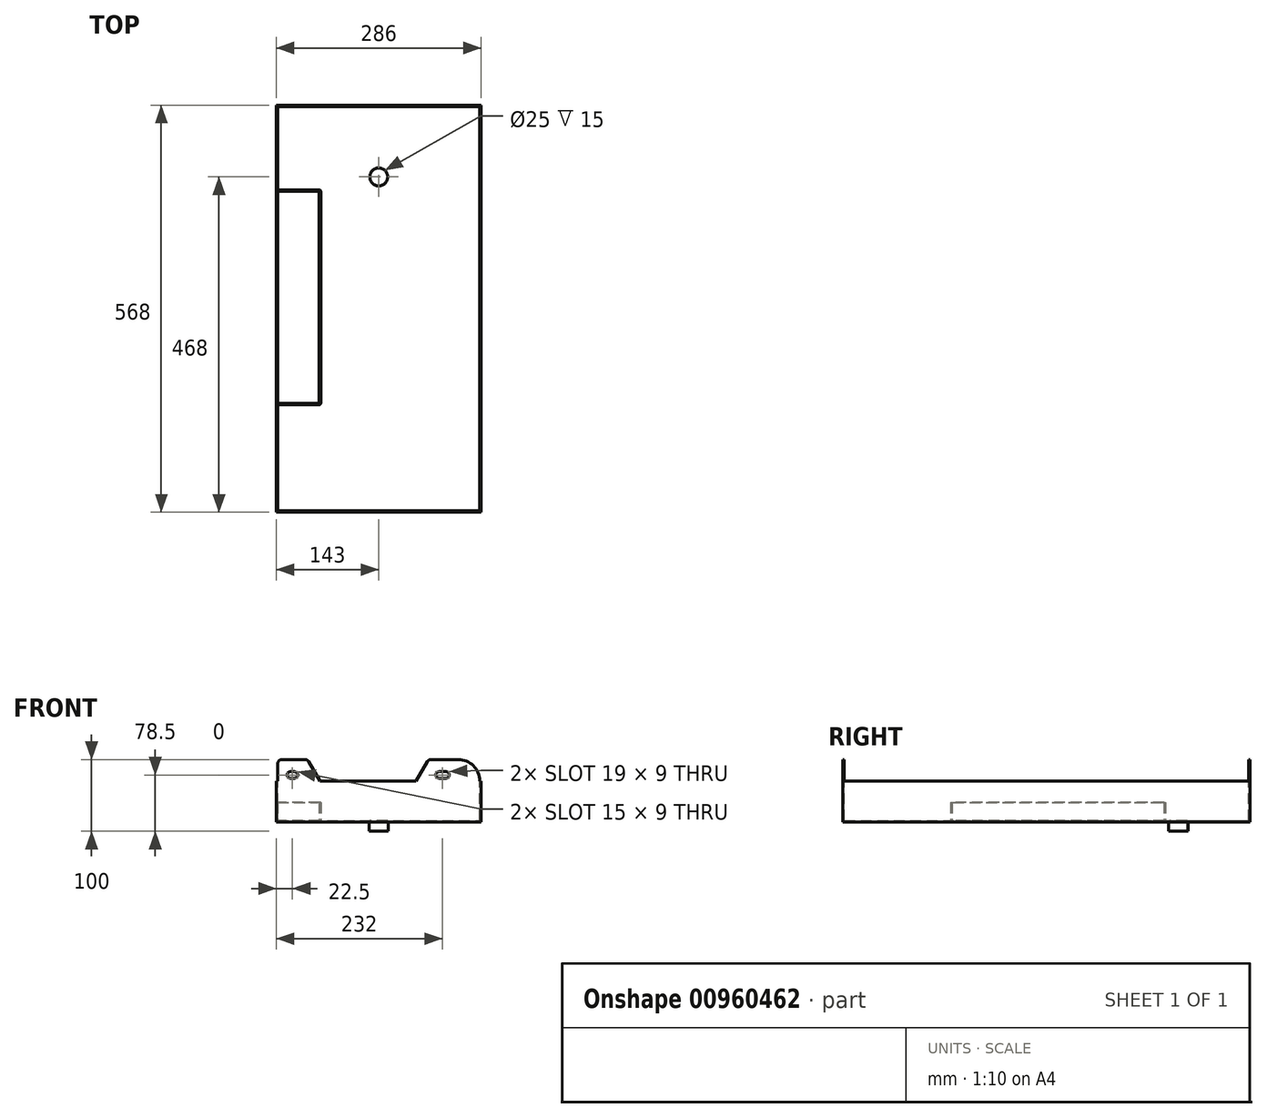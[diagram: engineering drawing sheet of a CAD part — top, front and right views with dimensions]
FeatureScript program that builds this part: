
annotation { "Feature Type Name" : "Feature", "Feature Type Description" : "" }
export const myFeature = defineFeature(function(context is Context, id is Id, definition is map)
    precondition{}
    {
        {
            var Q0;
            Q0=qCreatedBy(makeId("Front.planeOp"),FACE);
            var sketch = newSketch(context, id + "F0", { "sketchPlane" : qUnion([Q0])});
            skLineSegment(sketch, "E0", {"start": v(0, 0) * mm, "end": v(0, -55) * mm});
            skLineSegment(sketch, "E1", {"start": v(0, -55) * mm, "end": v(282, -55) * mm});
            skLineSegment(sketch, "E2", {"start": v(282, -55) * mm, "end": v(282, 0) * mm});
            skLineSegment(sketch, "E3", {"start": v(282, 0) * mm, "end": v(284, 0) * mm});
            skLineSegment(sketch, "E4", {"start": v(284, 0) * mm, "end": v(284, -57) * mm});
            skLineSegment(sketch, "E5", {"start": v(284, -57) * mm, "end": v(-2, -57) * mm});
            skLineSegment(sketch, "E6", {"start": v(-2, -57) * mm, "end": v(-2, 0) * mm});
            skLineSegment(sketch, "E7", {"start": v(-2, 0) * mm, "end": v(0, 0) * mm});
            skSolve(sketch);
        }
        {
            var Q0;
            Q0=makeQuery(id+"F0.imprint","IMPRINT",FACE,{"disambiguationData":[TD([[makeQuery(id+"F0.imprint","IMPRINT",EDGE,{"derivedFrom":sQuery(id+"F0.wireOp",EDGE,"E0")}),-1.0]])]});
            extrude(context, id + "F1", {"entities" : qUnion([Q0]), "depth" : 568 * mm, "offsetDistance" : 25 * mm});
        }
        {
            var Q0;
            Q0=qCreatedBy(makeId("Front.planeOp"),FACE);
            var sketch = newSketch(context, id + "F2", { "sketchPlane" : qUnion([Q0])});
            skLineSegment(sketch, "E8", {"start": v(0, 0) * mm, "end": v(0, 24) * mm});
            skLineSegment(sketch, "E9", {"start": v(0, 0) * mm, "end": v(0, -55) * mm});
            skLineSegment(sketch, "E10", {"start": v(6, 30) * mm, "end": v(38, 30) * mm});
            skLineSegment(sketch, "E11", {"start": v(43.2, 27) * mm, "end": v(58.78, 0) * mm});
            skLineSegment(sketch, "E12", {"start": v(0, -55) * mm, "end": v(282, -55) * mm});
            skLineSegment(sketch, "E13", {"start": v(282, -55) * mm, "end": v(282, 0) * mm});
            skLineSegment(sketch, "E14", {"start": v(252, 30) * mm, "end": v(214, 30) * mm});
            skLineSegment(sketch, "E15", {"start": v(208.8, 27) * mm, "end": v(193.22, 0) * mm});
            skLineSegment(sketch, "E16", {"start": v(193.22, 0) * mm, "end": v(58.78, 0) * mm});
            skPoint(sketch, "E17.visualSharp", {"position": v(0, 30) * mm});
            skArc(sketch, "E17.filletArc", {"start": v(6, 30) * mm, "mid": v(1.76, 28.24) * mm, "end": v(0, 24) * mm});
            skPoint(sketch, "E18.visualSharp", {"position": v(41.46, 30) * mm});
            skArc(sketch, "E18.filletArc", {"start": v(43.2, 27) * mm, "mid": v(41, 29.2) * mm, "end": v(38, 30) * mm});
            skPoint(sketch, "E19.visualSharp", {"position": v(282, 30) * mm});
            skArc(sketch, "E19.filletArc", {"start": v(282, 0) * mm, "mid": v(273.21, 21.21) * mm, "end": v(252, 30) * mm});
            skPoint(sketch, "E20.visualSharp", {"position": v(210.54, 30) * mm});
            skArc(sketch, "E20.filletArc", {"start": v(214, 30) * mm, "mid": v(211, 29.2) * mm, "end": v(208.8, 27) * mm});
            skPoint(sketch, "E21", {"position": v(17.5, 8.5) * mm});
            skPoint(sketch, "E22", {"position": v(23.5, 8.5) * mm});
            skPoint(sketch, "E23", {"position": v(225, 8.5) * mm});
            skPoint(sketch, "E24", {"position": v(235, 8.5) * mm});
            skArc(sketch, "E25", {"start": v(17.5, 13) * mm, "mid": v(13, 8.5) * mm, "end": v(17.5, 4) * mm});
            skArc(sketch, "E26", {"start": v(23.5, 4) * mm, "mid": v(28, 8.5) * mm, "end": v(23.5, 13) * mm});
            skLineSegment(sketch, "E27", {"start": v(17.5, 13) * mm, "end": v(23.5, 13) * mm});
            skLineSegment(sketch, "E28", {"start": v(17.5, 4) * mm, "end": v(23.5, 4) * mm});
            skArc(sketch, "E29", {"start": v(225, 13) * mm, "mid": v(220.5, 8.5) * mm, "end": v(225, 4) * mm});
            skArc(sketch, "E30", {"start": v(235, 4) * mm, "mid": v(239.5, 8.5) * mm, "end": v(235, 13) * mm});
            skLineSegment(sketch, "E31", {"start": v(225, 13) * mm, "end": v(235, 13) * mm});
            skLineSegment(sketch, "E32", {"start": v(235, 4) * mm, "end": v(225, 4) * mm});
            skSolve(sketch);
        }
        {
            var Q0;
            Q0=makeQuery(id+"F2.imprint","IMPRINT",FACE,{"disambiguationData":[TD([[makeQuery(id+"F2.imprint","IMPRINT",EDGE,{"derivedFrom":sQuery(id+"F2.wireOp",EDGE,"E8")}),-1.0]])]});
            extrude(context, id + "F3", {"entities" : qUnion([Q0]), "operationType" : NewBodyOperationType.ADD, "depth" : 2 * mm, "offsetDistance" : 25 * mm});
        }
        {
            var Q0;
            Q0=makeQuery(id+"F1.opExtrude","CAP_FACE",FACE,{"disambiguationData":[OSD([sQuery(id+"F0.wireOp",EDGE,"E0"),sQuery(id+"F0.wireOp",EDGE,"E1"),sQuery(id+"F0.wireOp",EDGE,"E2"),sQuery(id+"F0.wireOp",EDGE,"E3"),sQuery(id+"F0.wireOp",EDGE,"E4"),sQuery(id+"F0.wireOp",EDGE,"E5"),sQuery(id+"F0.wireOp",EDGE,"E6"),sQuery(id+"F0.wireOp",EDGE,"E7")])],"isStart":false});
            var sketch = newSketch(context, id + "F4", { "sketchPlane" : qUnion([Q0])});
            skLineSegment(sketch, "E33", {"start": v(0, -55) * mm, "end": v(0, 24) * mm});
            skLineSegment(sketch, "E34", {"start": v(6, 30) * mm, "end": v(38, 30) * mm});
            skLineSegment(sketch, "E35", {"start": v(43.2, 27) * mm, "end": v(58.78, 0) * mm});
            skLineSegment(sketch, "E36", {"start": v(58.78, 0) * mm, "end": v(193.22, 0) * mm});
            skLineSegment(sketch, "E37", {"start": v(193.22, 0) * mm, "end": v(208.8, 27) * mm});
            skLineSegment(sketch, "E38", {"start": v(214, 30) * mm, "end": v(252, 30) * mm});
            skLineSegment(sketch, "E39", {"start": v(282, 0) * mm, "end": v(282, -55) * mm});
            skLineSegment(sketch, "E40", {"start": v(282, -55) * mm, "end": v(0, -55) * mm});
            skPoint(sketch, "E41.visualSharp", {"position": v(41.46, 30) * mm});
            skArc(sketch, "E41.filletArc", {"start": v(43.2, 27) * mm, "mid": v(41, 29.2) * mm, "end": v(38, 30) * mm});
            skPoint(sketch, "E42.visualSharp", {"position": v(282, 30) * mm});
            skArc(sketch, "E42.filletArc", {"start": v(282, 0) * mm, "mid": v(273.21, 21.21) * mm, "end": v(252, 30) * mm});
            skPoint(sketch, "E43.visualSharp", {"position": v(0, 30) * mm});
            skArc(sketch, "E43.filletArc", {"start": v(6, 30) * mm, "mid": v(1.76, 28.24) * mm, "end": v(0, 24) * mm});
            skPoint(sketch, "E44.visualSharp", {"position": v(210.54, 30) * mm});
            skArc(sketch, "E44.filletArc", {"start": v(214, 30) * mm, "mid": v(211, 29.2) * mm, "end": v(208.8, 27) * mm});
            skPoint(sketch, "E45", {"position": v(17.5, 8.5) * mm});
            skPoint(sketch, "E46", {"position": v(23.5, 8.5) * mm});
            skPoint(sketch, "E47", {"position": v(225, 8.5) * mm});
            skPoint(sketch, "E48", {"position": v(235, 8.5) * mm});
            skArc(sketch, "E49", {"start": v(17.5, 13) * mm, "mid": v(13, 8.5) * mm, "end": v(17.5, 4) * mm});
            skArc(sketch, "E50", {"start": v(23.5, 4) * mm, "mid": v(28, 8.5) * mm, "end": v(23.5, 13) * mm});
            skLineSegment(sketch, "E51", {"start": v(17.5, 13) * mm, "end": v(23.5, 13) * mm});
            skLineSegment(sketch, "E52", {"start": v(17.5, 4) * mm, "end": v(23.5, 4) * mm});
            skArc(sketch, "E53", {"start": v(225, 13) * mm, "mid": v(220.5, 8.5) * mm, "end": v(225, 4) * mm});
            skArc(sketch, "E54", {"start": v(235, 4) * mm, "mid": v(239.5, 8.5) * mm, "end": v(235, 13) * mm});
            skLineSegment(sketch, "E55", {"start": v(225, 13) * mm, "end": v(235, 13) * mm});
            skLineSegment(sketch, "E56", {"start": v(225, 4) * mm, "end": v(235, 4) * mm});
            skSolve(sketch);
        }
        {
            var Q0;
            Q0=makeQuery(id+"F4.imprint","IMPRINT",FACE,{"disambiguationData":[TD([[makeQuery(id+"F4.imprint","IMPRINT",EDGE,{"derivedFrom":sQuery(id+"F4.wireOp",EDGE,"E34")}),-1.0]])]});
            extrude(context, id + "F5", {"entities" : qUnion([Q0]), "operationType" : NewBodyOperationType.ADD, "oppositeDirection" : true, "depth" : 2 * mm, "offsetDistance" : 25 * mm});
        }
        {
            var Q0;
            Q0=makeQuery(id+"F1.opExtrude","SWEPT_FACE",FACE,{"disambiguationData":[OSD([sQuery(id+"F0.wireOp",EDGE,"E1")])]});
            var sketch = newSketch(context, id + "F6", { "sketchPlane" : qUnion([Q0])});
            skPoint(sketch, "E57", {"position": v(98.7, 0) * mm});
            skPoint(sketch, "E58", {"position": v(141, -100) * mm});
            skCircle(sketch, "E59", {"center": v(141, -100) * mm, "radius": 12.5 * mm});
            skSolve(sketch);
        }
        {
            var Q0;
            Q0=makeQuery(id+"F6.imprint","IMPRINT",FACE,{"disambiguationData":[TD([[makeQuery(id+"F6.imprint","IMPRINT",EDGE,{"derivedFrom":sQuery(id+"F6.wireOp",EDGE,"E59")}),1.0]])]});
            extrude(context, id + "F7", {"entities" : qUnion([Q0]), "operationType" : NewBodyOperationType.REMOVE, "oppositeDirection" : true, "depth" : 25 * mm, "offsetDistance" : 25 * mm});
        }
        {
            var Q0;
            Q0=makeQuery(id+"F1.opExtrude","SWEPT_FACE",FACE,{"disambiguationData":[OSD([sQuery(id+"F0.wireOp",EDGE,"E5")])]});
            var sketch = newSketch(context, id + "F8", { "sketchPlane" : qUnion([Q0])});
            skCircle(sketch, "E60", {"center": v(141, 100) * mm, "radius": 13.5 * mm});
            skCircle(sketch, "E61", {"center": v(141, 100) * mm, "radius": 12.5 * mm});
            skSolve(sketch);
        }
        {
            var Q0;
            Q0=makeQuery(id+"F8.imprint","IMPRINT",FACE,{"disambiguationData":[TD([[makeQuery(id+"F8.imprint","IMPRINT",EDGE,{"derivedFrom":sQuery(id+"F8.wireOp",EDGE,"E60")}),1.0]])]});
            extrude(context, id + "F9", {"entities" : qUnion([Q0]), "operationType" : NewBodyOperationType.ADD, "depth" : 13 * mm, "offsetDistance" : 25 * mm});
        }
        {
            var Q0;
            Q0=makeQuery(id+"F1.opExtrude","SWEPT_FACE",FACE,{"disambiguationData":[OSD([sQuery(id+"F0.wireOp",EDGE,"E1")])]});
            var sketch = newSketch(context, id + "F10", { "sketchPlane" : qUnion([Q0])});
            skPoint(sketch, "E62", {"position": v(60, -418) * mm});
            skPoint(sketch, "E63", {"position": v(58, -416) * mm});
            skLineSegment(sketch, "E64", {"start": v(58, -118) * mm, "end": v(0, -118) * mm});
            skLineSegment(sketch, "E65", {"start": v(0, -120) * mm, "end": v(56, -120) * mm});
            skLineSegment(sketch, "E66", {"start": v(60, -120) * mm, "end": v(60, -416) * mm});
            skLineSegment(sketch, "E67", {"start": v(56, -416) * mm, "end": v(0, -416) * mm});
            skLineSegment(sketch, "E68", {"start": v(58, -414) * mm, "end": v(58, -122) * mm});
            skLineSegment(sketch, "E69", {"start": v(58, -418) * mm, "end": v(0, -418) * mm});
            skPoint(sketch, "E70.visualSharp", {"position": v(60, -118) * mm});
            skArc(sketch, "E70.filletArc", {"start": v(60, -120) * mm, "mid": v(59.41, -118.59) * mm, "end": v(58, -118) * mm});
            skArc(sketch, "E71.filletArc", {"start": v(58, -122) * mm, "mid": v(57.41, -120.59) * mm, "end": v(56, -120) * mm});
            skArc(sketch, "E72.filletArc", {"start": v(58, -418) * mm, "mid": v(59.41, -417.41) * mm, "end": v(60, -416) * mm});
            skArc(sketch, "E73.filletArc", {"start": v(56, -416) * mm, "mid": v(57.41, -415.41) * mm, "end": v(58, -414) * mm});
            skLineSegment(sketch, "E74", {"start": v(0, -416) * mm, "end": v(0, -418) * mm});
            skLineSegment(sketch, "E75", {"start": v(0, -118) * mm, "end": v(0, -120) * mm});
            skSolve(sketch);
        }
        {
            var Q0;
            {var subQ2=sQuery(id+"F10.wireOp",EDGE,"E64");Q0=makeQuery(id+"F10.imprint","IMPRINT",FACE,{"disambiguationData":[TD([[makeQuery(id+"F10.imprint","IMPRINT",EDGE,{"derivedFrom":subQ2}),1.0]])]});}
            extrude(context, id + "F11", {"entities" : qUnion([Q0]), "operationType" : NewBodyOperationType.ADD, "depth" : 25 * mm, "offsetDistance" : 25 * mm});
        }
        {
            var Q0;
            Q0=makeQuery(id+"F11.boolean.opBoolean","SPLIT",FACE,{"disambiguationData":[TD([makeQuery(id+"F11.opExtrude","SWEPT_FACE",FACE,{"disambiguationData":[OSD([sQuery(id+"F10.wireOp",EDGE,"E65")])]})])],"derivedFrom":makeQuery(id+"F1.opExtrude","SWEPT_FACE",FACE,{"disambiguationData":[OSD([sQuery(id+"F0.wireOp",EDGE,"E1")])]})});
            var sketch = newSketch(context, id + "F12", { "sketchPlane" : qUnion([Q0])});
            skLineSegment(sketch, "E76", {"start": v(56, -120) * mm, "end": v(56, -120) * mm});
            skLineSegment(sketch, "E77", {"start": v(58, -122) * mm, "end": v(58, -414) * mm});
            skLineSegment(sketch, "E78", {"start": v(0, -416) * mm, "end": v(56, -416) * mm});
            skArc(sketch, "E79", {"start": v(56, -416) * mm, "mid": v(57.41, -415.41) * mm, "end": v(58, -414) * mm});
            skArc(sketch, "E80", {"start": v(58, -122) * mm, "mid": v(57.41, -120.59) * mm, "end": v(56, -120) * mm});
            skLineSegment(sketch, "E81", {"start": v(0, -120) * mm, "end": v(56, -120) * mm});
            skSolve(sketch);
        }
        {
            var Q0;
            Q0=makeQuery(id+"F12.imprint","IMPRINT",FACE,{"disambiguationData":[TD([[makeQuery(id+"F12.imprint","IMPRINT",EDGE,{"derivedFrom":sQuery(id+"F12.wireOp",EDGE,"E77")}),1.0]])]});
            extrude(context, id + "F13", {"entities" : qUnion([Q0]), "operationType" : NewBodyOperationType.REMOVE, "oppositeDirection" : true, "depth" : 25 * mm, "offsetDistance" : 25 * mm});
        }
    });
